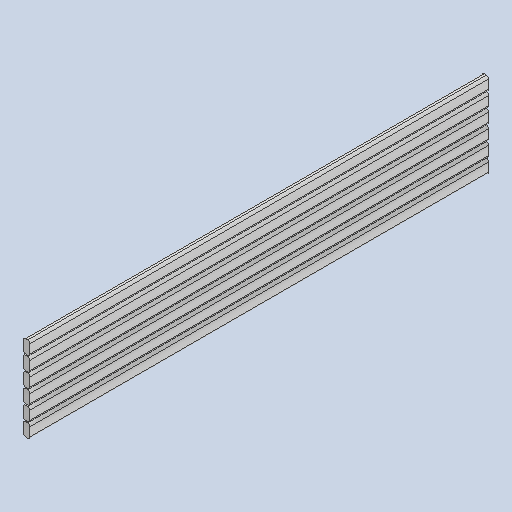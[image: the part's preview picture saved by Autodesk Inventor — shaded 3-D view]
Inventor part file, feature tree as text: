
AUTODESK INVENTOR PART (.ipt)
format: ipt  version: 2023 (Build 270158030, 158C)  size: 193,024 bytes
history: native  units: mm
features: other x4, extrude x1, sketch x1, reference x1
ambient origin geometry x8: Origin, YZ Plane, XZ Plane, XY Plane, X Axis, Y Axis, Z Axis, Center Point
bodies: Body1 (feature_tree)
feature tree (7):
  other  "slats"
  extrude  "Extrusion1"  [1 undecoded]
  sketch  "Sketch1"  dims[d0=2000.0mm d1=75.0mm d2=0.0mm d3=0.0mm]
  reference  "Reference1"
  other  "<userpath>\Documents\0004-inventor\3D-CAD-main\primary-engineer-bench.iam"
  other  "primary-engineer-bench.iam"
  other  "bench-end-peice:1"
note: 1 required parameter value undecoded (feature->parameter linkage not recoverable at this tier; creation-order binding heuristic only, values carry confidence <= 0.55)
